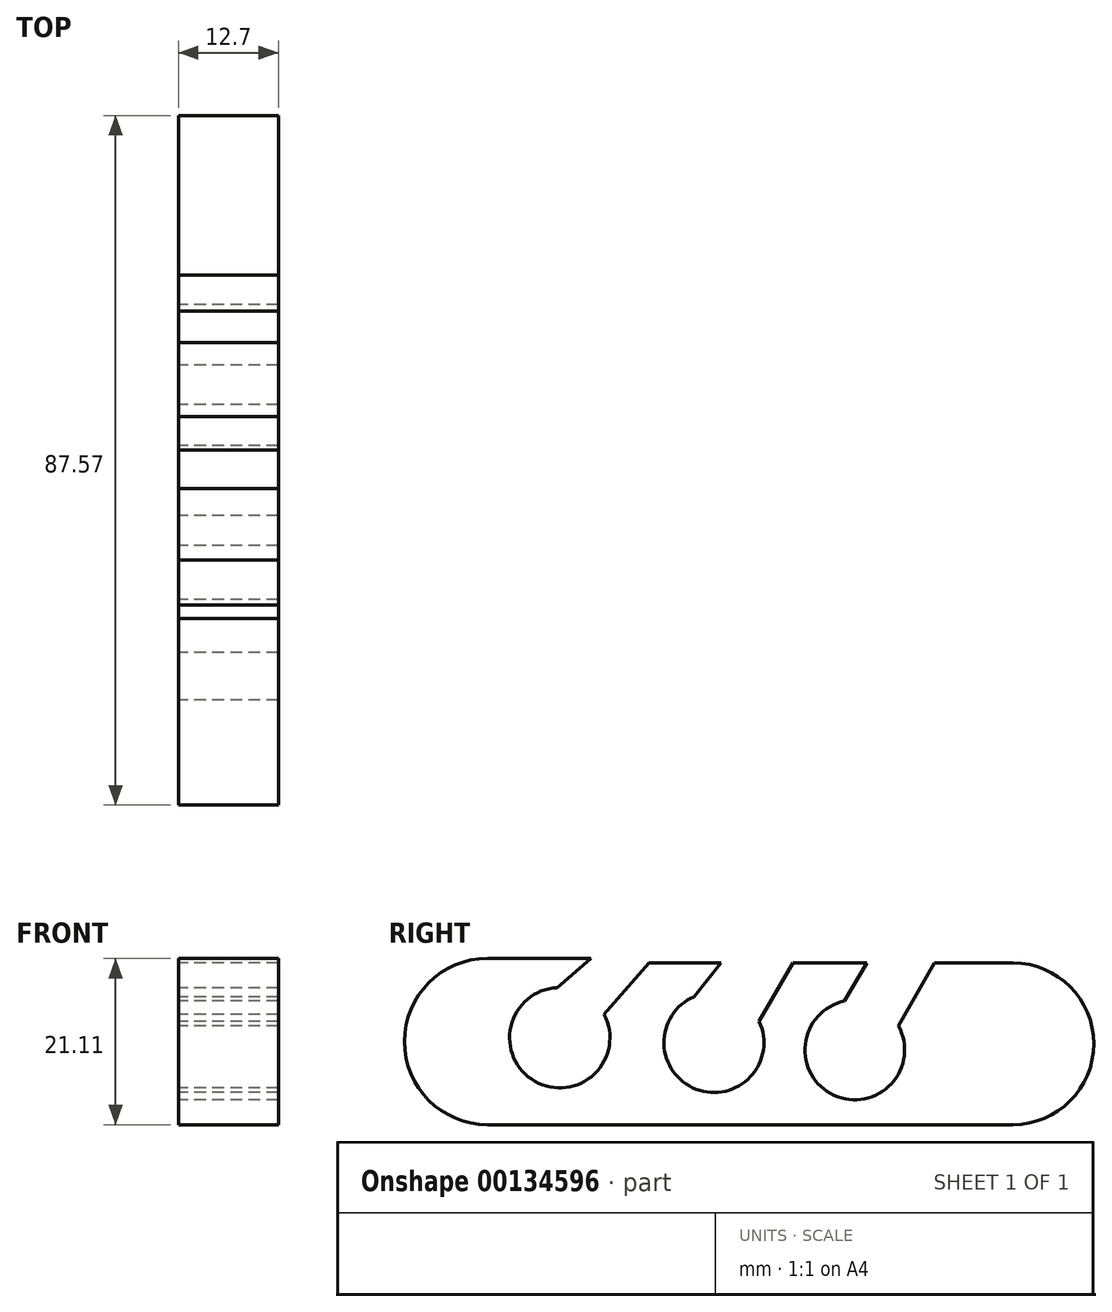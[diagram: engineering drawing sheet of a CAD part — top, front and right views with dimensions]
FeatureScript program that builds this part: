
annotation { "Feature Type Name" : "Feature", "Feature Type Description" : "" }
export const myFeature = defineFeature(function(context is Context, id is Id, definition is map)
    precondition{}
    {
        {
            var Q0;
            Q0=qCreatedBy(makeId("Right.planeOp"),FACE);
            var sketch = newSketch(context, id + "F0", { "sketchPlane" : qUnion([Q0])});
            skLineSegment(sketch, "E0", {"start": v(-34.51, 17.54) * mm, "end": v(-21.4, 17.54) * mm});
            skLineSegment(sketch, "E1", {"start": v(-21.4, 17.54) * mm, "end": v(-25.67, 13.83) * mm});
            skArc(sketch, "E2", {"start": v(-25.67, 13.83) * mm, "mid": v(-28.5, 1.94) * mm, "end": v(-19.68, 10.41) * mm});
            skLineSegment(sketch, "E3", {"start": v(-19.68, 10.41) * mm, "end": v(-13.98, 16.97) * mm});
            skLineSegment(sketch, "E4", {"start": v(-13.98, 16.97) * mm, "end": v(-4.85, 16.97) * mm});
            skLineSegment(sketch, "E5", {"start": v(-4.85, 16.97) * mm, "end": v(-8.27, 12.7) * mm});
            skArc(sketch, "E6", {"start": v(-8.27, 12.7) * mm, "mid": v(-8, 0.93) * mm, "end": v(0, 9.56) * mm});
            skLineSegment(sketch, "E7", {"start": v(0, 9.56) * mm, "end": v(4.28, 16.97) * mm});
            skLineSegment(sketch, "E8", {"start": v(4.28, 16.97) * mm, "end": v(13.7, 16.97) * mm});
            skLineSegment(sketch, "E9", {"start": v(13.7, 16.97) * mm, "end": v(10.84, 12.12) * mm});
            skArc(sketch, "E10", {"start": v(10.84, 12.12) * mm, "mid": v(9.5, 0.18) * mm, "end": v(17.68, 8.99) * mm});
            skLineSegment(sketch, "E11", {"start": v(17.68, 8.99) * mm, "end": v(22.25, 16.97) * mm});
            skPoint(sketch, "E11.endSnap0", {"position": v(-9.41, 16.97) * mm});
            skLineSegment(sketch, "E12", {"start": v(22.25, 16.97) * mm, "end": v(32.23, 16.97) * mm});
            skArc(sketch, "E13", {"start": v(32.23, -3.57) * mm, "mid": v(42.5, 6.7) * mm, "end": v(32.23, 16.97) * mm});
            skLineSegment(sketch, "E14", {"start": v(32.23, -3.57) * mm, "end": v(-34.51, -3.57) * mm});
            skArc(sketch, "E15", {"start": v(-34.51, 17.54) * mm, "mid": v(-45.07, 6.99) * mm, "end": v(-34.51, -3.57) * mm});
            skSolve(sketch);
        }
        {
            var Q0;
            Q0=makeQuery(id+"F0.imprint","IMPRINT",FACE,{"disambiguationData":[TD([[makeQuery(id+"F0.imprint","IMPRINT",EDGE,{"derivedFrom":sQuery(id+"F0.wireOp",EDGE,"E0")}),-1.0]])]});
            extrude(context, id + "F1", {"entities" : qUnion([Q0]), "depth" : 12.7 * mm});
        }
    });
